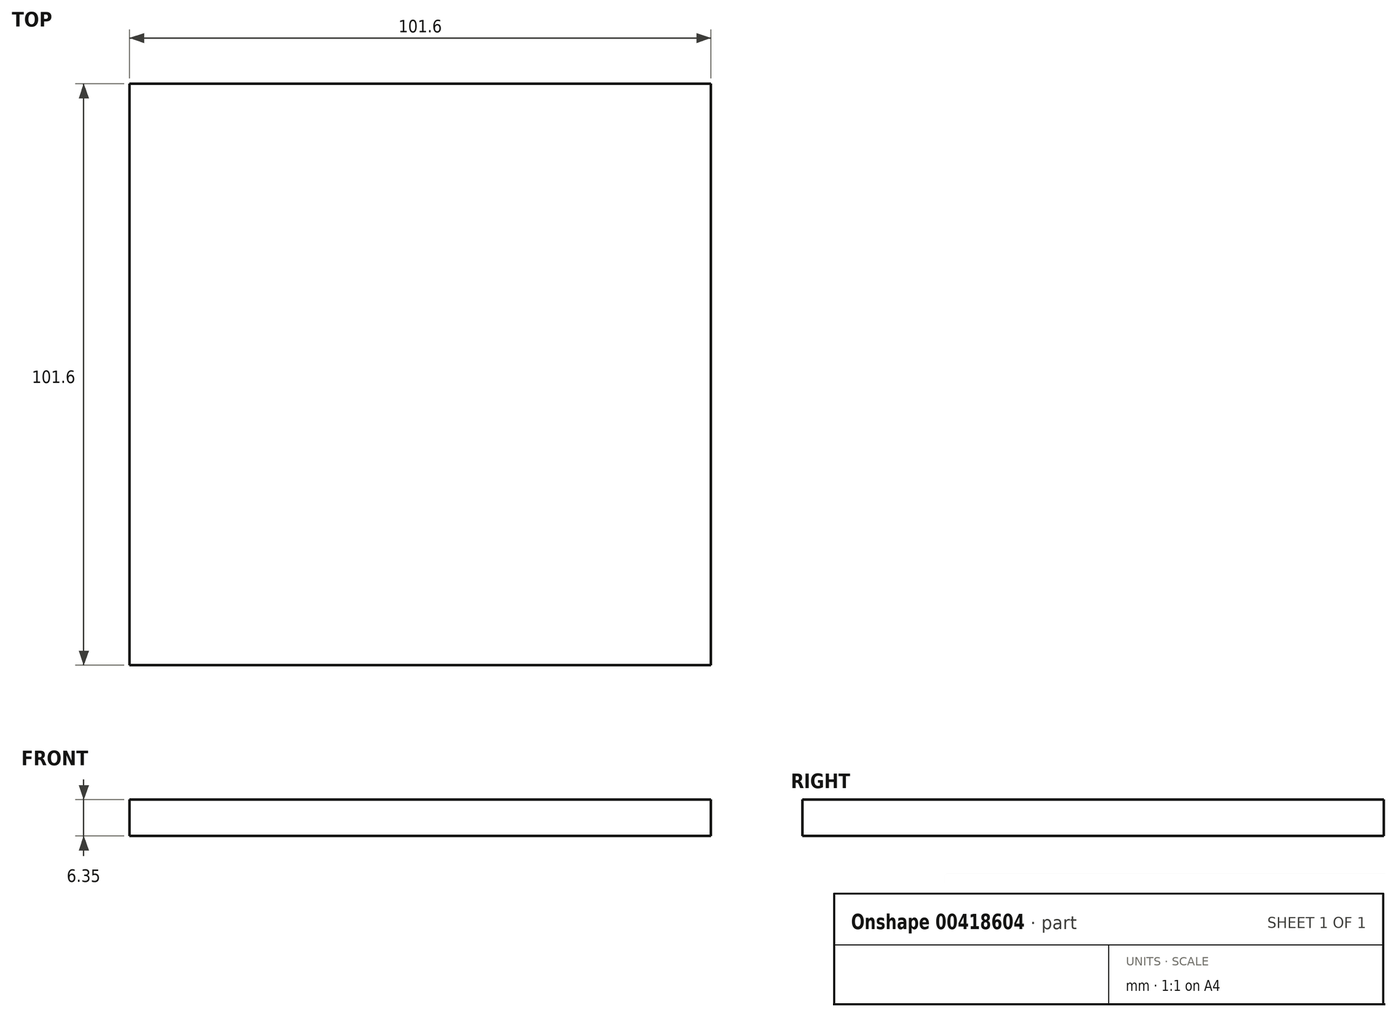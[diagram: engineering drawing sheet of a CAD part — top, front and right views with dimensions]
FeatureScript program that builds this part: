
annotation { "Feature Type Name" : "Feature", "Feature Type Description" : "" }
export const myFeature = defineFeature(function(context is Context, id is Id, definition is map)
    precondition{}
    {
        {
            var Q0;
            Q0=qCreatedBy(makeId("Top.planeOp"),FACE);
            var sketch = newSketch(context, id + "F0", { "sketchPlane" : qUnion([Q0])});
            skLineSegment(sketch, "E0.bottom", {"start": v(0, 0) * mm, "end": v(-101.6, 0) * mm});
            skLineSegment(sketch, "E0.top", {"start": v(0, -101.6) * mm, "end": v(-101.6, -101.6) * mm});
            skLineSegment(sketch, "E0.left", {"start": v(0, 0) * mm, "end": v(0, -101.6) * mm});
            skLineSegment(sketch, "E0.right", {"start": v(-101.6, 0) * mm, "end": v(-101.6, -101.6) * mm});
            skSolve(sketch);
        }
        {
            var Q0;
            Q0 = qSketchRegion(id + "F0", true);
            extrude(context, id + "F1", {"entities" : qUnion([Q0]), "depth" : 6.35 * mm});
        }
    });
